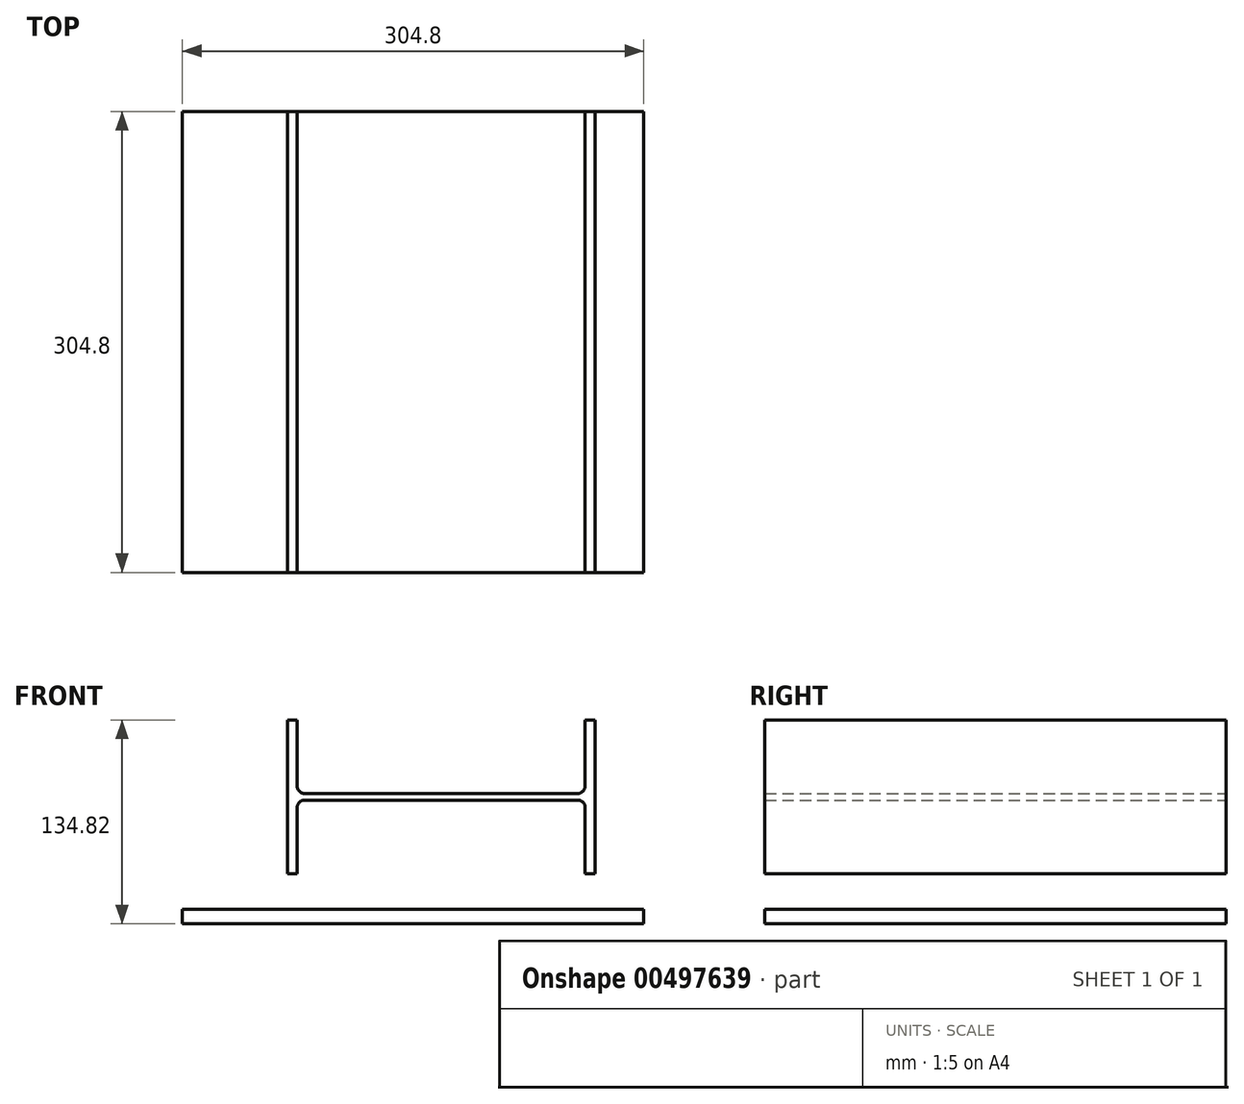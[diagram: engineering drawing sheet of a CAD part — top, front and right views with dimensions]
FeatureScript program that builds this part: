
annotation { "Feature Type Name" : "Feature", "Feature Type Description" : "" }
export const myFeature = defineFeature(function(context is Context, id is Id, definition is map)
    precondition{}
    {
        {
            var Q0;
            Q0=qCreatedBy(makeId("Front.planeOp"),FACE);
            var sketch = newSketch(context, id + "F0", { "sketchPlane" : qUnion([Q0])});
            skLineSegment(sketch, "E0.bottom", {"start": v(101.6, -50.8) * mm, "end": v(95.12, -50.8) * mm});
            skLineSegment(sketch, "E0.top", {"start": v(101.6, 50.8) * mm, "end": v(95.12, 50.8) * mm});
            skLineSegment(sketch, "E0.left", {"start": v(101.6, -50.8) * mm, "end": v(101.6, 50.8) * mm});
            skLineSegment(sketch, "E0.right", {"start": v(-101.6, -50.8) * mm, "end": v(-101.6, 50.8) * mm});
            skPoint(sketch, "E0.middle", {"position": v(0, 0) * mm});
            skLineSegment(sketch, "E1", {"start": v(-95.12, 2.16) * mm, "end": v(95.12, 2.16) * mm});
            skLineSegment(sketch, "E2", {"start": v(95.12, -2.16) * mm, "end": v(-95.12, -2.16) * mm});
            skLineSegment(sketch, "E3.0", {"start": v(-95.12, -50.8) * mm, "end": v(-95.12, -2.16) * mm});
            skLineSegment(sketch, "E4.0", {"start": v(95.12, -50.8) * mm, "end": v(95.12, -2.16) * mm});
            skLineSegment(sketch, "E5.trimOffspring", {"start": v(-95.12, 50.8) * mm, "end": v(-101.6, 50.8) * mm});
            skLineSegment(sketch, "E6.trimOffspring", {"start": v(95.12, 2.16) * mm, "end": v(95.12, 50.8) * mm});
            skLineSegment(sketch, "E7.trimOffspring", {"start": v(-95.12, -50.8) * mm, "end": v(-101.6, -50.8) * mm});
            skLineSegment(sketch, "E8.trimOffspring", {"start": v(-95.12, 2.16) * mm, "end": v(-95.12, 50.8) * mm});
            skSolve(sketch);
        }
        {
            var Q0;
            Q0 = qSketchRegion(id + "F0", true);
            extrude(context, id + "F1", {"entities" : qUnion([Q0]), "endBound" : BoundingType.SYMMETRIC, "depth" : 304.8 * mm});
        }
        {
            var Q0;
            Q0=makeQuery(id+"F1.opExtrude","SWEPT_EDGE",EDGE,{"disambiguationData":[OSD([sQuery(id+"F0.wireOp",EDGE,"E1"),sQuery(id+"F0.wireOp",EDGE,"E8.trimOffspring")])]});
            var Q1;
            Q1=makeQuery(id+"F1.opExtrude","SWEPT_EDGE",EDGE,{"disambiguationData":[OSD([sQuery(id+"F0.wireOp",EDGE,"E2"),sQuery(id+"F0.wireOp",EDGE,"E3.0")])]});
            var Q2;
            Q2=makeQuery(id+"F1.opExtrude","SWEPT_EDGE",EDGE,{"disambiguationData":[OSD([sQuery(id+"F0.wireOp",EDGE,"E2"),sQuery(id+"F0.wireOp",EDGE,"E4.0")])]});
            var Q3;
            Q3=makeQuery(id+"F1.opExtrude","SWEPT_EDGE",EDGE,{"disambiguationData":[OSD([sQuery(id+"F0.wireOp",EDGE,"E1"),sQuery(id+"F0.wireOp",EDGE,"E6.trimOffspring")])]});
            fillet(context, id + "F2", {"entities" : qUnion([Q0, Q1, Q2, Q3]), "radius" : 5.08 * mm, "tangentPropagation" : true, "allowEdgeOverflow" : false});
        }
        {
            var Q0;
            Q0=qCreatedBy(makeId("Front.planeOp"),FACE);
            var sketch = newSketch(context, id + "F3", { "sketchPlane" : qUnion([Q0])});
            skLineSegment(sketch, "E9.bottom", {"start": v(133.92, -84.02) * mm, "end": v(-170.88, -84.02) * mm});
            skLineSegment(sketch, "E9.top", {"start": v(133.92, -74.5) * mm, "end": v(-170.88, -74.5) * mm});
            skLineSegment(sketch, "E9.left", {"start": v(133.92, -84.02) * mm, "end": v(133.92, -74.5) * mm});
            skLineSegment(sketch, "E9.right", {"start": v(-170.88, -84.02) * mm, "end": v(-170.88, -74.5) * mm});
            skPoint(sketch, "E9.middle", {"position": v(-18.48, -79.25) * mm});
            skSolve(sketch);
        }
        {
            var Q0;
            Q0 = qSketchRegion(id + "F3", true);
            extrude(context, id + "F4", {"entities" : qUnion([Q0]), "endBound" : BoundingType.SYMMETRIC, "depth" : 304.8 * mm});
        }
    });
